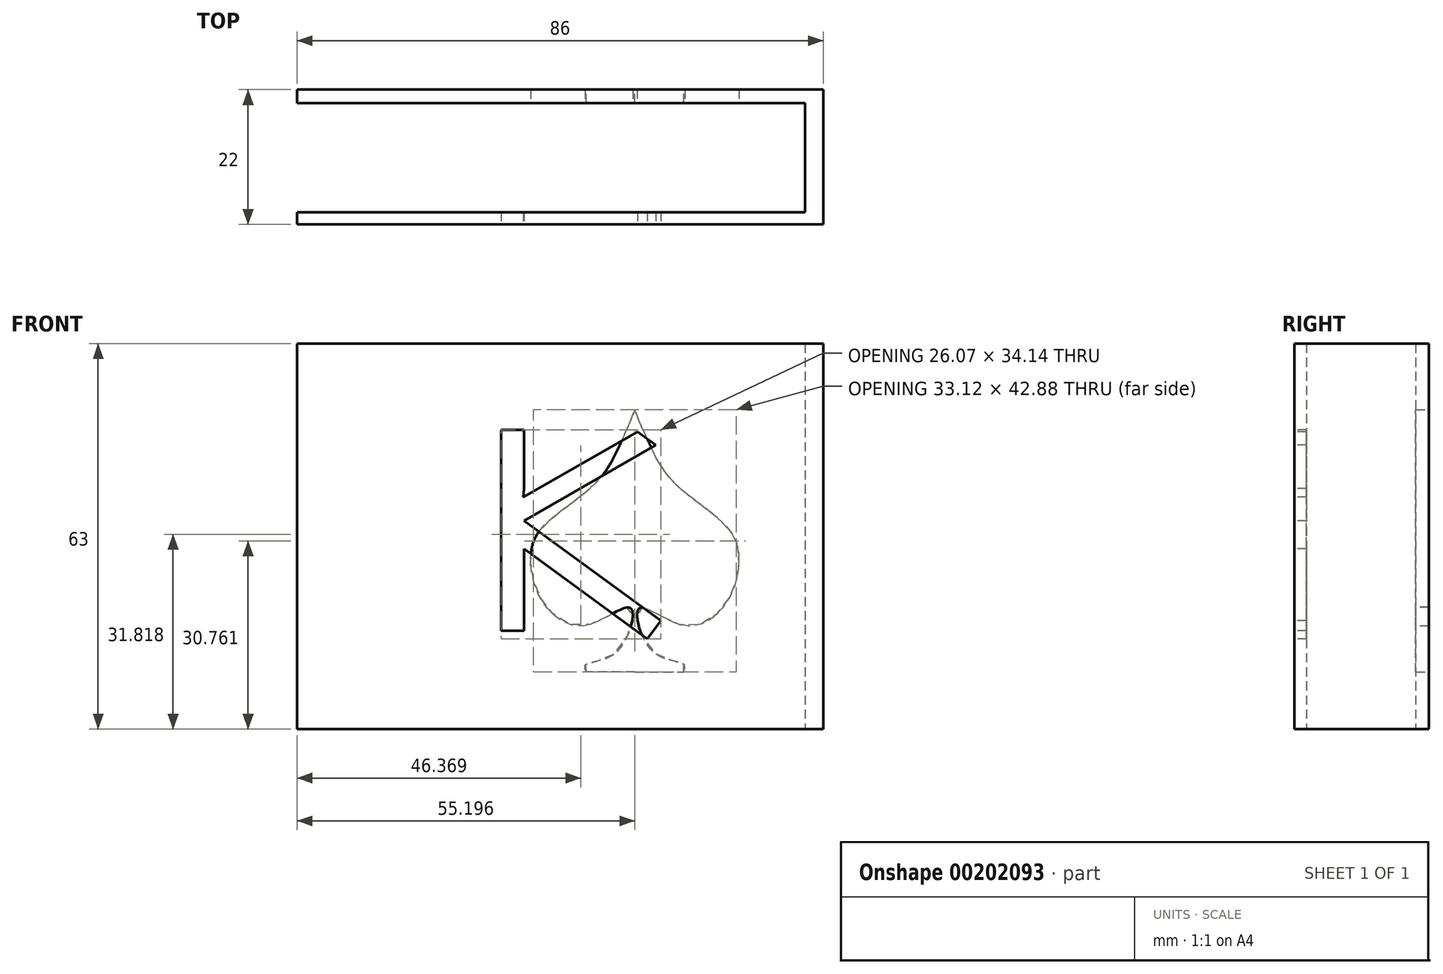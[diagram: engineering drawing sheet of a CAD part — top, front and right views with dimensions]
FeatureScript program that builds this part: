
annotation { "Feature Type Name" : "Feature", "Feature Type Description" : "" }
export const myFeature = defineFeature(function(context is Context, id is Id, definition is map)
    precondition{}
    {
        {
            var Q0;
            Q0=qCreatedBy(makeId("Front.planeOp"),FACE);
            var sketch = newSketch(context, id + "F0", { "sketchPlane" : qUnion([Q0])});
            skLineSegment(sketch, "E0", {"start": v(-40.05, -31.5) * mm, "end": v(45.95, -31.5) * mm});
            skLineSegment(sketch, "E1", {"start": v(45.95, -31.5) * mm, "end": v(45.95, 31.5) * mm});
            skLineSegment(sketch, "E2", {"start": v(45.95, 31.5) * mm, "end": v(-40.05, 31.5) * mm});
            skLineSegment(sketch, "E3", {"start": v(-40.05, 31.5) * mm, "end": v(-40.05, -31.5) * mm});
            skSolve(sketch);
        }
        {
            var Q0;
            Q0 = qSketchRegion(id + "F0", true);
            extrude(context, id + "F1", {"entities" : qUnion([Q0]), "depth" : 22 * mm});
        }
        {
            var Q0;
            Q0=makeQuery(id+"F1.opExtrude","SWEPT_FACE",FACE,{"disambiguationData":[OSD([sQuery(id+"F0.wireOp",EDGE,"E0")])]});
            var sketch = newSketch(context, id + "F2", { "sketchPlane" : qUnion([Q0])});
            skLineSegment(sketch, "E4", {"start": v(-40.05, 20.02) * mm, "end": v(42.97, 20.02) * mm});
            skLineSegment(sketch, "E5", {"start": v(42.97, 20.02) * mm, "end": v(42.97, 2.19) * mm});
            skLineSegment(sketch, "E6", {"start": v(42.97, 2.19) * mm, "end": v(-40.05, 2.19) * mm});
            skSolve(sketch);
        }
        {
            var Q0;
            Q0 = qSketchRegion(id + "F2", true);
            var Q1;
            {var subQ0=sQuery(id+"F2.wireOp",EDGE,"E4");Q1=makeQuery(id+"F2.imprint","IMPRINT",FACE,{"disambiguationData":[TD([[makeQuery(id+"F2.imprint","IMPRINT",EDGE,{"derivedFrom":subQ0}),-1.0]])]});}
            extrude(context, id + "F3", {"entities" : qUnion([Q0, Q1]), "operationType" : NewBodyOperationType.REMOVE, "oppositeDirection" : true, "depth" : 76.2 * mm});
        }
        {
            var Q0;
            Q0=makeQuery(id+"F1.opExtrude","CAP_FACE",FACE,{"disambiguationData":[OSD([sQuery(id+"F0.wireOp",EDGE,"E0"),sQuery(id+"F0.wireOp",EDGE,"E1"),sQuery(id+"F0.wireOp",EDGE,"E2"),sQuery(id+"F0.wireOp",EDGE,"E3")])],"isStart":true});
            var sketch = newSketch(context, id + "F4", { "sketchPlane" : qUnion([Q0])});
            skLineSegment(sketch, "E7", {"start": v(-45.95, 31.5) * mm, "end": v(-37.33, 22.19) * mm});
            skLineSegment(sketch, "E8", {"start": v(-45.95, -31.5) * mm, "end": v(-37.33, -22.17) * mm});
            skLineSegment(sketch, "E9", {"start": v(-15.15, -22.17) * mm, "end": v(-7.18, -22.17) * mm});
            skFitSpline(sketch, "E10", {"points": [v(-7.18, -22.17) * mm, v(-7.18, -20.89) * mm, v(-12.09, -18.94) * mm, v(-14.42, -11.7) * mm, v(-7.18, -14.55) * mm, v(0, -10.54) * mm, v(1.87, -3.56) * mm, v(0, 1.48) * mm, v(-8.86, 8.85) * mm, v(-13.25, 16.22) * mm, v(-15.2, 21) * mm, v(-15.15, 21.27) * mm, v(-15.15, 21) * mm], "startDerivative": vector(10.64, 34.71) * mm, "endDerivative": vector(-1.17, -19.3) * mm});
            skLineSegment(sketch, "E11", {"start": v(-15.14, 21.13) * mm, "end": v(-15.15, -22.17) * mm});
            skLineSegment(sketch, "E12.MirrorCS", {"start": v(-15.15, -22.17) * mm, "end": v(-23.12, -22.16) * mm});
            skFitSpline(sketch, "E13.MirrorCS", {"points": [v(-23.12, -22.16) * mm, v(-23.12, -20.88) * mm, v(-18.2, -18.94) * mm, v(-15.88, -11.7) * mm, v(-23.12, -14.55) * mm, v(-30.3, -10.54) * mm, v(-32.17, -3.56) * mm, v(-30.3, 1.49) * mm, v(-21.43, 8.86) * mm, v(-17.03, 16.22) * mm, v(-15.1, 21) * mm, v(-15.13, 21.27) * mm, v(-15.13, 21) * mm], "startDerivative": vector(-10.63, 34.72) * mm, "endDerivative": vector(1.16, -19.3) * mm});
            skSolve(sketch);
        }
        {
            var Q0;
            {var subQ0=sQuery(id+"F4.wireOp",EDGE,"E9");Q0=makeQuery(id+"F4.imprint","IMPRINT",FACE,{"disambiguationData":[TD([[makeQuery(id+"F4.imprint","IMPRINT",EDGE,{"derivedFrom":subQ0}),1.0]])]});}
            var Q1;
            {var subQ0=sQuery(id+"F4.wireOp",EDGE,"E12.MirrorCS");Q1=makeQuery(id+"F4.imprint","IMPRINT",FACE,{"disambiguationData":[TD([[makeQuery(id+"F4.imprint","IMPRINT",EDGE,{"derivedFrom":subQ0}),-1.0]])]});}
            extrude(context, id + "F5", {"entities" : qUnion([Q0, Q1]), "operationType" : NewBodyOperationType.REMOVE, "oppositeDirection" : true, "depth" : 12.7 * mm});
        }
        {
            var Q0;
            Q0=makeQuery(id+"F1.opExtrude","CAP_FACE",FACE,{"disambiguationData":[OSD([sQuery(id+"F0.wireOp",EDGE,"E0"),sQuery(id+"F0.wireOp",EDGE,"E1"),sQuery(id+"F0.wireOp",EDGE,"E2"),sQuery(id+"F0.wireOp",EDGE,"E3")])],"isStart":false});
            var sketch = newSketch(context, id + "F6", { "sketchPlane" : qUnion([Q0])});
            skLineSegment(sketch, "E14", {"start": v(-6.72, 17.39) * mm, "end": v(-6.72, -15.42) * mm});
            skLineSegment(sketch, "E15", {"start": v(-6.72, -15.42) * mm, "end": v(-3, -15.42) * mm});
            skLineSegment(sketch, "E16", {"start": v(-3, -15.42) * mm, "end": v(-3, -2.03) * mm});
            skLineSegment(sketch, "E17", {"start": v(-3, 7.81) * mm, "end": v(-3, 17.4) * mm});
            skLineSegment(sketch, "E18", {"start": v(-3, 17.4) * mm, "end": v(-6.72, 17.39) * mm});
            skPoint(sketch, "E19.end.orphan", {"position": v(15.45, 19.43) * mm});
            skPoint(sketch, "E20.end.orphan", {"position": v(15.45, -15.42) * mm});
            skLineSegment(sketch, "E21", {"start": v(-3, 2.58) * mm, "end": v(19.35, -13.73) * mm});
            skLineSegment(sketch, "E22", {"start": v(19.35, -13.73) * mm, "end": v(17.16, -16.74) * mm});
            skPoint(sketch, "E23.startSnap0", {"position": v(-4.85, -15.42) * mm});
            skPoint(sketch, "E23.start.orphan", {"position": v(-4.85, -20.65) * mm});
            skLineSegment(sketch, "E24", {"start": v(17.16, -16.74) * mm, "end": v(-3, -2.03) * mm});
            skPoint(sketch, "E25.orphan", {"position": v(-3, -1.14) * mm});
            skLineSegment(sketch, "E26", {"start": v(-3, 2.58) * mm, "end": v(18.56, 14.9) * mm});
            skLineSegment(sketch, "E27", {"start": v(18.56, 14.9) * mm, "end": v(15.55, 17.1) * mm});
            skLineSegment(sketch, "E28", {"start": v(15.55, 17.1) * mm, "end": v(-3.1, 6.43) * mm});
            skLineSegment(sketch, "E29", {"start": v(-3.1, 6.43) * mm, "end": v(-3, 7.81) * mm});
            skSolve(sketch);
        }
        {
            var Q0;
            Q0=makeQuery(id+"F6.imprint","IMPRINT",FACE,{"disambiguationData":[TD([[makeQuery(id+"F6.imprint","IMPRINT",EDGE,{"derivedFrom":sQuery(id+"F6.wireOp",EDGE,"E14")}),1.0]])]});
            extrude(context, id + "F7", {"entities" : qUnion([Q0]), "operationType" : NewBodyOperationType.REMOVE, "oppositeDirection" : true, "depth" : 12.7 * mm});
        }
    });
